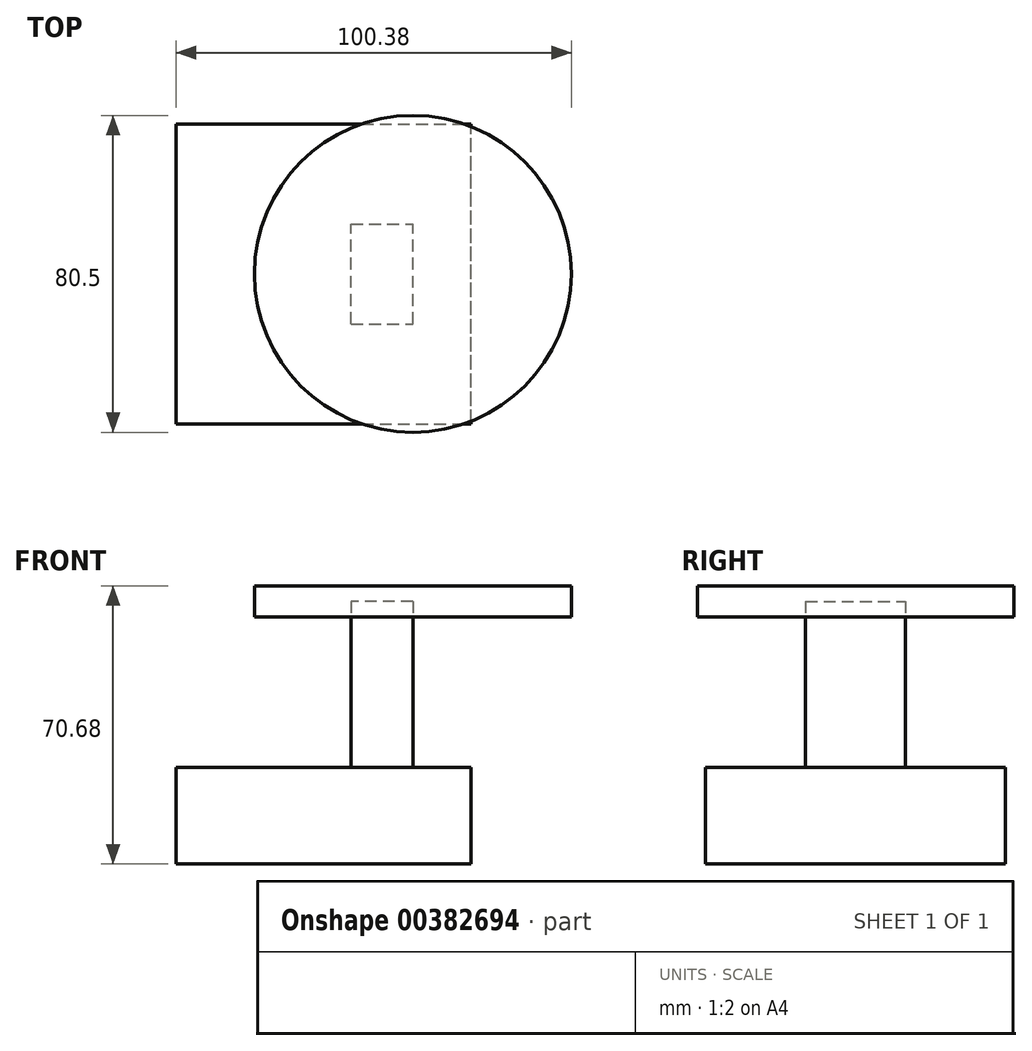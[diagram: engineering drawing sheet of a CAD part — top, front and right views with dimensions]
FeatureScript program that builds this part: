
annotation { "Feature Type Name" : "Feature", "Feature Type Description" : "" }
export const myFeature = defineFeature(function(context is Context, id is Id, definition is map)
    precondition{}
    {
        {
            var Q0;
            Q0=qCreatedBy(makeId("Front.planeOp"),FACE);
            var sketch = newSketch(context, id + "F0", { "sketchPlane" : qUnion([Q0])});
            skLineSegment(sketch, "E0.bottom", {"start": v(-37.43, 12.27) * mm, "end": v(37.43, 12.27) * mm});
            skLineSegment(sketch, "E0.top", {"start": v(-37.43, -12.27) * mm, "end": v(37.43, -12.27) * mm});
            skLineSegment(sketch, "E0.left", {"start": v(-37.43, 12.27) * mm, "end": v(-37.43, -12.27) * mm});
            skLineSegment(sketch, "E0.right", {"start": v(37.43, 12.27) * mm, "end": v(37.43, -12.27) * mm});
            skPoint(sketch, "E0.middle", {"position": v(0, 0) * mm});
            skLineSegment(sketch, "E1.bottom", {"start": v(22.7, 54.49) * mm, "end": v(7, 54.49) * mm});
            skLineSegment(sketch, "E1.top", {"start": v(22.7, 12.27) * mm, "end": v(7, 12.27) * mm});
            skLineSegment(sketch, "E1.left", {"start": v(22.7, 54.49) * mm, "end": v(22.7, 12.27) * mm});
            skLineSegment(sketch, "E1.right", {"start": v(7, 54.49) * mm, "end": v(7, 12.27) * mm});
            skPoint(sketch, "E1.middle", {"position": v(14.85, 33.38) * mm});
            skLineSegment(sketch, "E2.bottom", {"start": v(22.7, 58.41) * mm, "end": v(62.95, 58.41) * mm});
            skLineSegment(sketch, "E2.top", {"start": v(22.7, 50.56) * mm, "end": v(62.95, 50.56) * mm});
            skLineSegment(sketch, "E2.left", {"start": v(22.7, 58.41) * mm, "end": v(22.7, 50.56) * mm});
            skLineSegment(sketch, "E2.right", {"start": v(62.95, 58.41) * mm, "end": v(62.95, 50.56) * mm});
            skPoint(sketch, "E2.middle", {"position": v(42.83, 54.49) * mm});
            skSolve(sketch);
        }
        {
            var Q0;
            Q0=makeQuery(id+"F0.imprint","IMPRINT",FACE,{"disambiguationData":[TD([[makeQuery(id+"F0.imprint","IMPRINT",EDGE,{"derivedFrom":sQuery(id+"F0.wireOp",EDGE,"E0.top")}),1.0]])]});
            extrude(context, id + "F1", {"entities" : qUnion([Q0]), "endBound" : BoundingType.SYMMETRIC, "depth" : 76.2 * mm});
        }
        {
            var Q0;
            {var subQ1=sQuery(id+"F0.wireOp",EDGE,"E1.bottom");Q0=makeQuery(id+"F0.imprint","IMPRINT",FACE,{"disambiguationData":[TD([[makeQuery(id+"F0.imprint","IMPRINT",EDGE,{"derivedFrom":subQ1}),1.0]])]});}
            extrude(context, id + "F2", {"entities" : qUnion([Q0]), "operationType" : NewBodyOperationType.ADD, "endBound" : BoundingType.SYMMETRIC, "depth" : 25.4 * mm});
        }
        {
            var Q0;
            {var subQ3=sQuery(id+"F0.wireOp",EDGE,"E2.bottom");Q0=makeQuery(id+"F0.imprint","IMPRINT",FACE,{"disambiguationData":[TD([[makeQuery(id+"F0.imprint","IMPRINT",EDGE,{"derivedFrom":subQ3}),-1.0]])]});}
            var Q1;
            Q1=sQuery(id+"F0.wireOp",EDGE,"E1.left");
            revolve(context, id + "F3", {"entities" : qUnion([Q0]), "axis" : qUnion([Q1]), "revolveType" : RevolveType.FULL});
        }
    });
